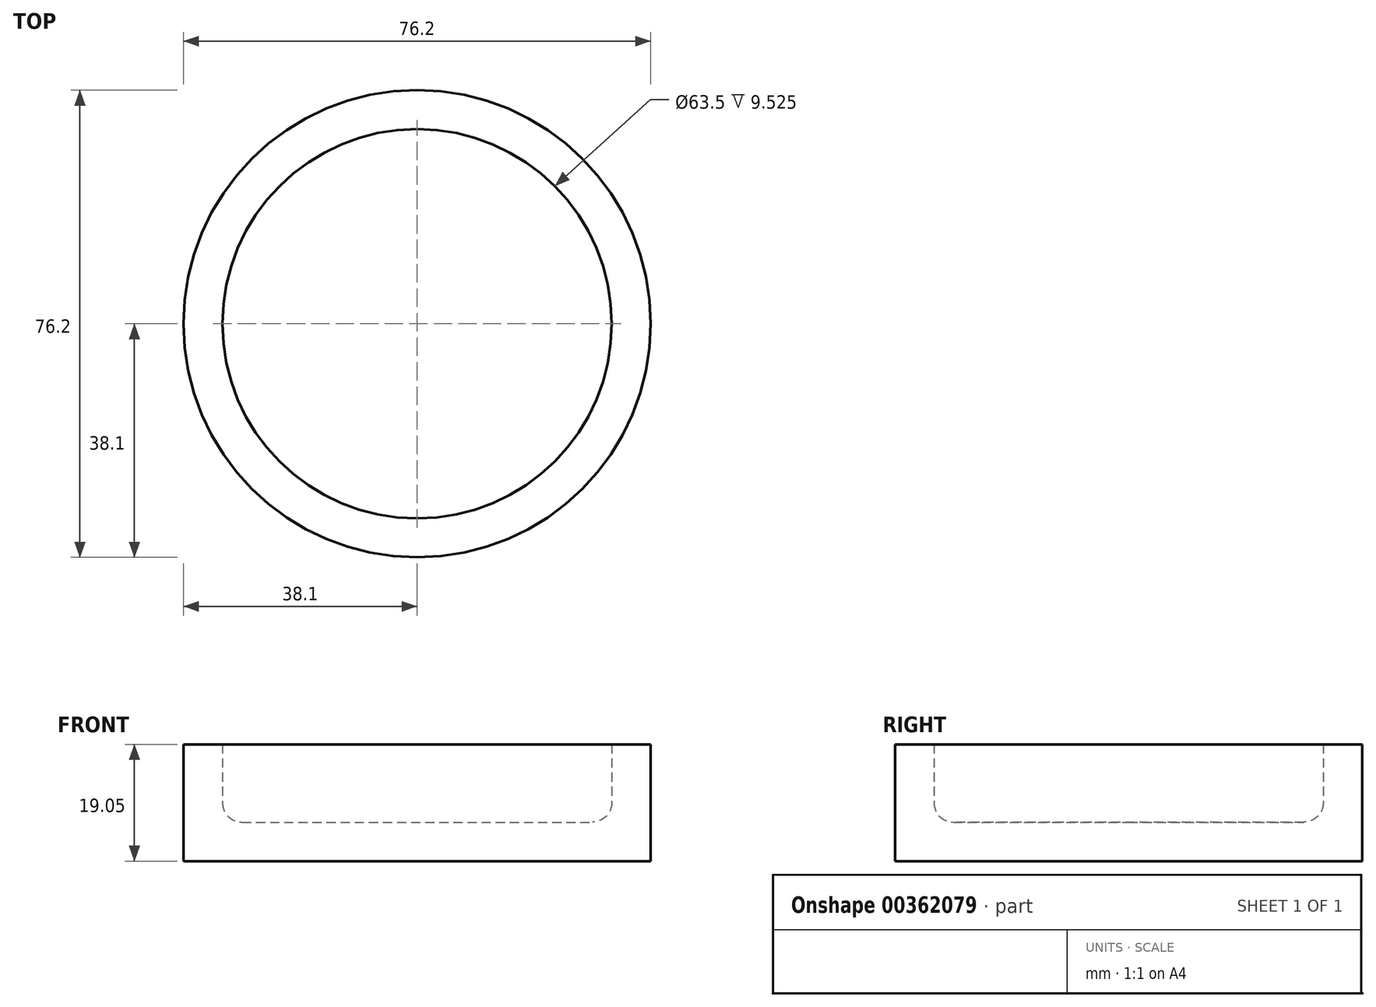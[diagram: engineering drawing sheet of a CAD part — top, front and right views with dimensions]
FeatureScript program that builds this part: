
annotation { "Feature Type Name" : "Feature", "Feature Type Description" : "" }
export const myFeature = defineFeature(function(context is Context, id is Id, definition is map)
    precondition{}
    {
        {
            var Q0;
            Q0=qCreatedBy(makeId("Front.planeOp"),FACE);
            var sketch = newSketch(context, id + "F0", { "sketchPlane" : qUnion([Q0])});
            skLineSegment(sketch, "E0", {"start": v(0, 6.35) * mm, "end": v(0, 0) * mm});
            skLineSegment(sketch, "E1.bottom", {"start": v(0, 0) * mm, "end": v(38.1, 0) * mm});
            skLineSegment(sketch, "E1.top", {"start": v(0, 6.35) * mm, "end": v(38.1, 6.35) * mm});
            skLineSegment(sketch, "E1.left", {"start": v(0, 0) * mm, "end": v(0, 6.35) * mm});
            skLineSegment(sketch, "E1.right", {"start": v(38.1, 0) * mm, "end": v(38.1, 6.35) * mm});
            skLineSegment(sketch, "E2.bottom", {"start": v(38.1, 6.35) * mm, "end": v(31.75, 6.35) * mm});
            skLineSegment(sketch, "E2.top", {"start": v(38.1, 19.05) * mm, "end": v(31.75, 19.05) * mm});
            skLineSegment(sketch, "E2.left", {"start": v(38.1, 6.35) * mm, "end": v(38.1, 19.05) * mm});
            skLineSegment(sketch, "E2.right", {"start": v(31.75, 6.35) * mm, "end": v(31.75, 19.05) * mm});
            skPoint(sketch, "E3.orphan", {"position": v(0, 32.71) * mm});
            skSolve(sketch);
        }
        {
            var Q0;
            Q0 = qSketchRegion(id + "F0", true);
            var Q1;
            Q1=sQuery(id+"F0.wireOp",EDGE,"E1.left");
            revolve(context, id + "F1", {"entities" : qUnion([Q0]), "axis" : qUnion([Q1]), "revolveType" : RevolveType.FULL});
        }
        {
            var Q0;
            Q0=makeQuery(id+"F1.opRevolve","SWEPT_EDGE",EDGE,{"disambiguationData":[OSD([sQuery(id+"F0.wireOp",EDGE,"E1.top"),sQuery(id+"F0.wireOp",EDGE,"E2.bottom"),sQuery(id+"F0.wireOp",EDGE,"E2.right")])]});
            fillet(context, id + "F2", {"entities" : qUnion([Q0]), "radius" : 3.17 * mm, "tangentPropagation" : true, "allowEdgeOverflow" : false});
        }
    });
